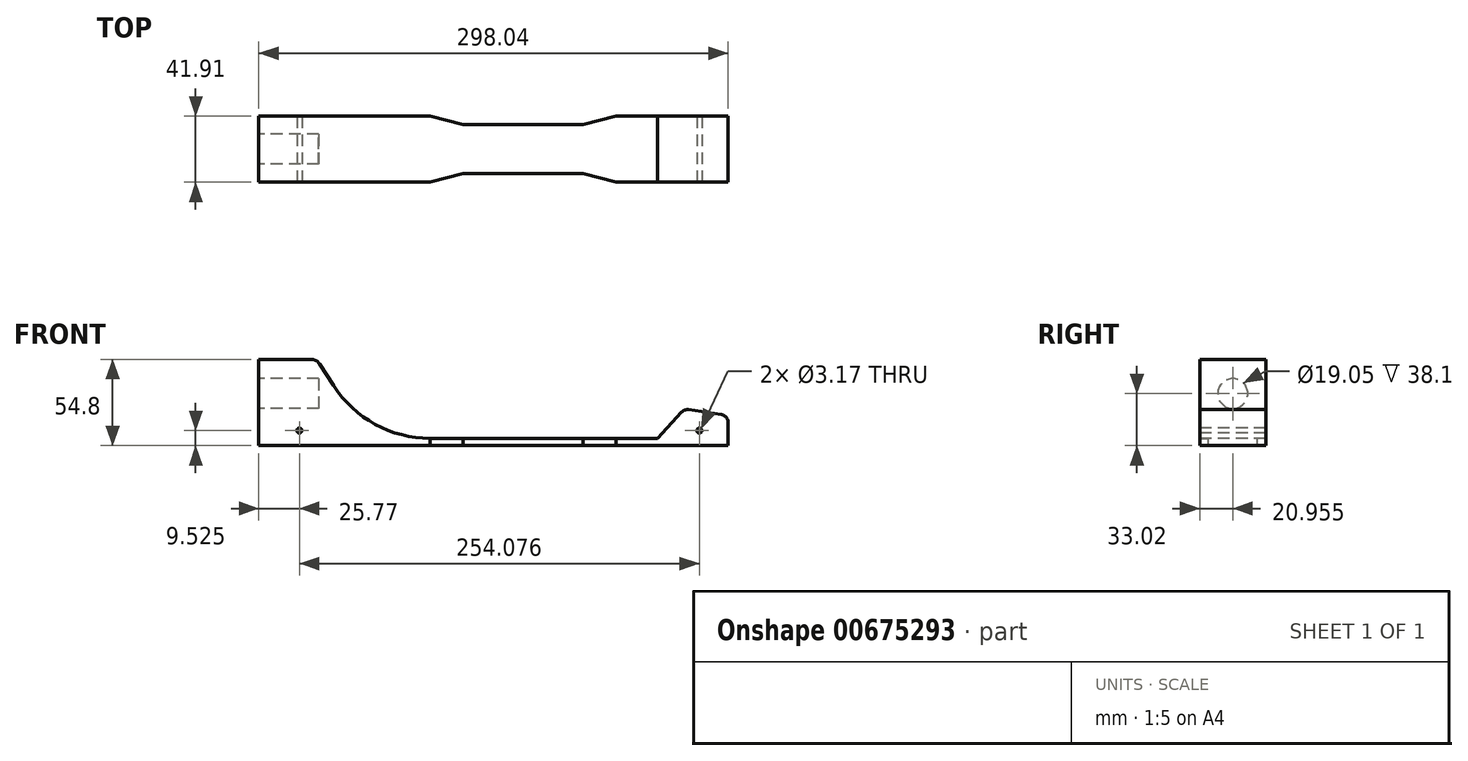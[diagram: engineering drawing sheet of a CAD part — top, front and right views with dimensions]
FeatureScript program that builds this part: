
annotation { "Feature Type Name" : "Feature", "Feature Type Description" : "" }
export const myFeature = defineFeature(function(context is Context, id is Id, definition is map)
    precondition{}
    {
        {
            var Q0;
            Q0=qCreatedBy(makeId("Front.planeOp"),FACE);
            var sketch = newSketch(context, id + "F0", { "sketchPlane" : qUnion([Q0])});
            skLineSegment(sketch, "E0", {"start": v(0, 0) * mm, "end": v(301.12, 0) * mm});
            skLineSegment(sketch, "E1", {"start": v(0, 0) * mm, "end": v(0, 62.72) * mm});
            skLineSegment(sketch, "E2", {"start": v(301.12, 0) * mm, "end": v(301.12, 19.05) * mm});
            skLineSegment(sketch, "E3", {"start": v(0, 62.72) * mm, "end": v(301.12, 19.05) * mm});
            skSolve(sketch);
        }
        {
            var Q0;
            Q0 = qSketchRegion(id + "F0", true);
            extrude(context, id + "F1", {"entities" : qUnion([Q0]), "oppositeDirection" : true, "depth" : 41.9 * mm, "offsetDistance" : 25.4 * mm});
        }
        {
            var Q0;
            Q0=makeQuery(id+"F1.opExtrude","SWEPT_FACE",FACE,{"disambiguationData":[OSD([sQuery(id+"F0.wireOp",EDGE,"E1")])]});
            var sketch = newSketch(context, id + "F2", { "sketchPlane" : qUnion([Q0])});
            skCircle(sketch, "E4", {"center": v(-20.96, 33.02) * mm, "radius": 9.52 * mm});
            skSolve(sketch);
        }
        {
            var Q0;
            Q0 = qSketchRegion(id + "F2", true);
            extrude(context, id + "F3", {"entities" : qUnion([Q0]), "operationType" : NewBodyOperationType.REMOVE, "oppositeDirection" : true, "depth" : 38.1 * mm, "offsetDistance" : 25.4 * mm});
        }
        {
            var Q0;
            Q0=makeQuery(id+"F1.opExtrude","CAP_FACE",FACE,{"disambiguationData":[OSD([sQuery(id+"F0.wireOp",EDGE,"E0"),sQuery(id+"F0.wireOp",EDGE,"E1"),sQuery(id+"F0.wireOp",EDGE,"E2"),sQuery(id+"F0.wireOp",EDGE,"E3")])],"isStart":true});
            var sketch = newSketch(context, id + "F4", { "sketchPlane" : qUnion([Q0])});
            skCircle(sketch, "E5", {"center": v(279.85, 9.53) * mm, "radius": 1.59 * mm});
            skPoint(sketch, "E5.centerSnap0", {"position": v(301.12, 9.53) * mm});
            skCircle(sketch, "E6", {"center": v(25.77, 9.53) * mm, "radius": 1.59 * mm});
            skSolve(sketch);
        }
        {
            var Q0;
            Q0=makeQuery(id+"F4.imprint","IMPRINT",FACE,{"disambiguationData":[TD([[makeQuery(id+"F4.imprint","IMPRINT",EDGE,{"derivedFrom":makeQuery(id+"F1.opExtrude","CAP_EDGE",EDGE,{"disambiguationData":[OSD([sQuery(id+"F0.wireOp",EDGE,"E0")])],"isStart":true})}),1.0]])]});
            var sketch = newSketch(context, id + "F5", { "sketchPlane" : qUnion([Q0])});
            skLineSegment(sketch, "E7", {"start": v(68.96, 4.6) * mm, "end": v(253.11, 4.6) * mm});
            skLineSegment(sketch, "E8", {"start": v(253.11, 4.6) * mm, "end": v(270.4, 23.2) * mm});
            skLineSegment(sketch, "E9", {"start": v(270.4, 23.2) * mm, "end": v(298.04, 19.09) * mm});
            skLineSegment(sketch, "E10", {"start": v(298.04, 19.09) * mm, "end": v(298.04, 0) * mm});
            skLineSegment(sketch, "E11", {"start": v(298.04, 0) * mm, "end": v(0, 0) * mm});
            skLineSegment(sketch, "E12", {"start": v(68.96, 4.6) * mm, "end": v(36.67, 54.8) * mm});
            skLineSegment(sketch, "E13", {"start": v(36.67, 54.8) * mm, "end": v(0, 54.8) * mm});
            skLineSegment(sketch, "E14", {"start": v(0, 54.8) * mm, "end": v(0, 0) * mm});
            skSolve(sketch);
        }
        {
            var Q0;
            Q0=makeQuery(id+"F5.imprint","IMPRINT",FACE,{"disambiguationData":[TD([[makeQuery(id+"F5.imprint","IMPRINT",EDGE,{"derivedFrom":sQuery(id+"F5.wireOp",EDGE,"E7")}),1.0]])]});
            extrude(context, id + "F6", {"entities" : qUnion([Q0]), "operationType" : NewBodyOperationType.REMOVE, "oppositeDirection" : true, "depth" : 41.9 * mm, "offsetDistance" : 25.4 * mm});
        }
        {
            var Q0;
            Q0=makeQuery(id+"F6.boolean.opBoolean","COPY",EDGE,{"derivedFrom":makeQuery(id+"F6.opExtrude","SWEPT_EDGE",EDGE,{"disambiguationData":[OSD([sQuery(id+"F5.wireOp",EDGE,"E7"),sQuery(id+"F5.wireOp",EDGE,"E12")])]})});
            fillet(context, id + "F7", {"entities" : qUnion([Q0]), "radius" : 72.98 * mm, "tangentPropagation" : true, "allowEdgeOverflow" : false});
        }
        {
            var Q0;
            Q0=makeQuery(id+"F6.boolean.opBoolean","COPY",EDGE,{"derivedFrom":makeQuery(id+"F6.opExtrude","SWEPT_EDGE",EDGE,{"disambiguationData":[OSD([sQuery(id+"F5.wireOp",EDGE,"E12"),sQuery(id+"F5.wireOp",EDGE,"E13")])]})});
            var Q1;
            Q1=makeQuery(id+"F6.boolean.opBoolean","COPY",EDGE,{"derivedFrom":makeQuery(id+"F6.opExtrude","SWEPT_EDGE",EDGE,{"disambiguationData":[OSD([sQuery(id+"F0.wireOp",EDGE,"E1"),sQuery(id+"F5.wireOp",EDGE,"E13"),sQuery(id+"F5.wireOp",EDGE,"E14")])]})});
            fillet(context, id + "F8", {"entities" : qUnion([Q0, Q1]), "radius" : 6.35 * mm, "tangentPropagation" : true, "allowEdgeOverflow" : false});
        }
        {
            var Q0;
            Q0=makeQuery(id+"F4.imprint","IMPRINT",FACE,{"disambiguationData":[TD([[makeQuery(id+"F4.imprint","IMPRINT",EDGE,{"derivedFrom":sQuery(id+"F4.wireOp",EDGE,"E5")}),1.0]])]});
            extrude(context, id + "F9", {"entities" : qUnion([Q0]), "operationType" : NewBodyOperationType.REMOVE, "oppositeDirection" : true, "depth" : 128.27 * mm, "offsetDistance" : 25.4 * mm});
        }
        {
            var Q0;
            Q0 = qSketchRegion(id + "F4", true);
            extrude(context, id + "F10", {"entities" : qUnion([Q0]), "operationType" : NewBodyOperationType.REMOVE, "oppositeDirection" : true, "depth" : 90.68 * mm, "offsetDistance" : 25.4 * mm});
        }
        {
            var Q0;
            Q0=makeQuery(id+"F6.boolean.opBoolean","COPY",EDGE,{"derivedFrom":makeQuery(id+"F6.opExtrude","SWEPT_EDGE",EDGE,{"disambiguationData":[OSD([sQuery(id+"F5.wireOp",EDGE,"E9"),sQuery(id+"F5.wireOp",EDGE,"E10")])]})});
            var Q1;
            Q1=makeQuery(id+"F6.boolean.opBoolean","COPY",EDGE,{"derivedFrom":makeQuery(id+"F6.opExtrude","SWEPT_EDGE",EDGE,{"disambiguationData":[OSD([sQuery(id+"F5.wireOp",EDGE,"E8"),sQuery(id+"F5.wireOp",EDGE,"E9")])]})});
            var Q2;
            Q2=makeQuery(id+"F6.boolean.opBoolean","COPY",EDGE,{"derivedFrom":makeQuery(id+"F6.opExtrude","CAP_EDGE",EDGE,{"disambiguationData":[OSD([sQuery(id+"F5.wireOp",EDGE,"E9")])],"isStart":false})});
            var Q3;
            Q3=makeQuery(id+"F6.boolean.opBoolean","COPY",EDGE,{"derivedFrom":makeQuery(id+"F6.opExtrude","CAP_EDGE",EDGE,{"disambiguationData":[OSD([sQuery(id+"F5.wireOp",EDGE,"E9")])],"isStart":true})});
            var Q4;
            Q4=makeQuery(id+"F6.boolean.opBoolean","COPY",EDGE,{"derivedFrom":makeQuery(id+"F6.opExtrude","SWEPT_EDGE",EDGE,{"disambiguationData":[OSD([sQuery(id+"F0.wireOp",EDGE,"E0"),sQuery(id+"F5.wireOp",EDGE,"E10"),sQuery(id+"F5.wireOp",EDGE,"E11")])]})});
            fillet(context, id + "F11", {"entities" : qUnion([Q0, Q1, Q2, Q3, Q4]), "radius" : 5.08 * mm, "tangentPropagation" : true, "allowEdgeOverflow" : false});
        }
        {
            var Q0;
            Q0=makeQuery(id+"F6.boolean.opBoolean","COPY",FACE,{"derivedFrom":makeQuery(id+"F6.opExtrude","SWEPT_FACE",FACE,{"disambiguationData":[OSD([sQuery(id+"F5.wireOp",EDGE,"E7")])]})});
            var sketch = newSketch(context, id + "F12", { "sketchPlane" : qUnion([Q0])});
            skLineSegment(sketch, "E15", {"start": v(253.11, 41.91) * mm, "end": v(226.78, 41.91) * mm});
            skLineSegment(sketch, "E16", {"start": v(226.78, 41.91) * mm, "end": v(205.88, 36.47) * mm});
            skLineSegment(sketch, "E17", {"start": v(205.88, 36.47) * mm, "end": v(129.68, 36.47) * mm});
            skLineSegment(sketch, "E18", {"start": v(129.68, 36.47) * mm, "end": v(108.79, 41.91) * mm});
            skLineSegment(sketch, "E19", {"start": v(253.11, 0) * mm, "end": v(226.78, 0) * mm});
            skLineSegment(sketch, "E20", {"start": v(226.78, 0) * mm, "end": v(205.88, 5.44) * mm});
            skLineSegment(sketch, "E21", {"start": v(205.88, 5.44) * mm, "end": v(129.68, 5.44) * mm});
            skLineSegment(sketch, "E22", {"start": v(129.68, 5.44) * mm, "end": v(108.79, 0) * mm});
            skSolve(sketch);
        }
        {
            var Q0;
            {var subQ0=sQuery(id+"F12.wireOp",EDGE,"E20");Q0=makeQuery(id+"F12.imprint","IMPRINT",FACE,{"disambiguationData":[TD([[makeQuery(id+"F12.imprint","IMPRINT",EDGE,{"derivedFrom":subQ0}),1.0]])]});}
            var Q1;
            {var subQ0=sQuery(id+"F12.wireOp",EDGE,"E16");Q1=makeQuery(id+"F12.imprint","IMPRINT",FACE,{"disambiguationData":[TD([[makeQuery(id+"F12.imprint","IMPRINT",EDGE,{"derivedFrom":subQ0}),-1.0]])]});}
            extrude(context, id + "F13", {"entities" : qUnion([Q0, Q1]), "operationType" : NewBodyOperationType.REMOVE, "oppositeDirection" : true, "depth" : 39.62 * mm, "offsetDistance" : 25.4 * mm});
        }
    });
